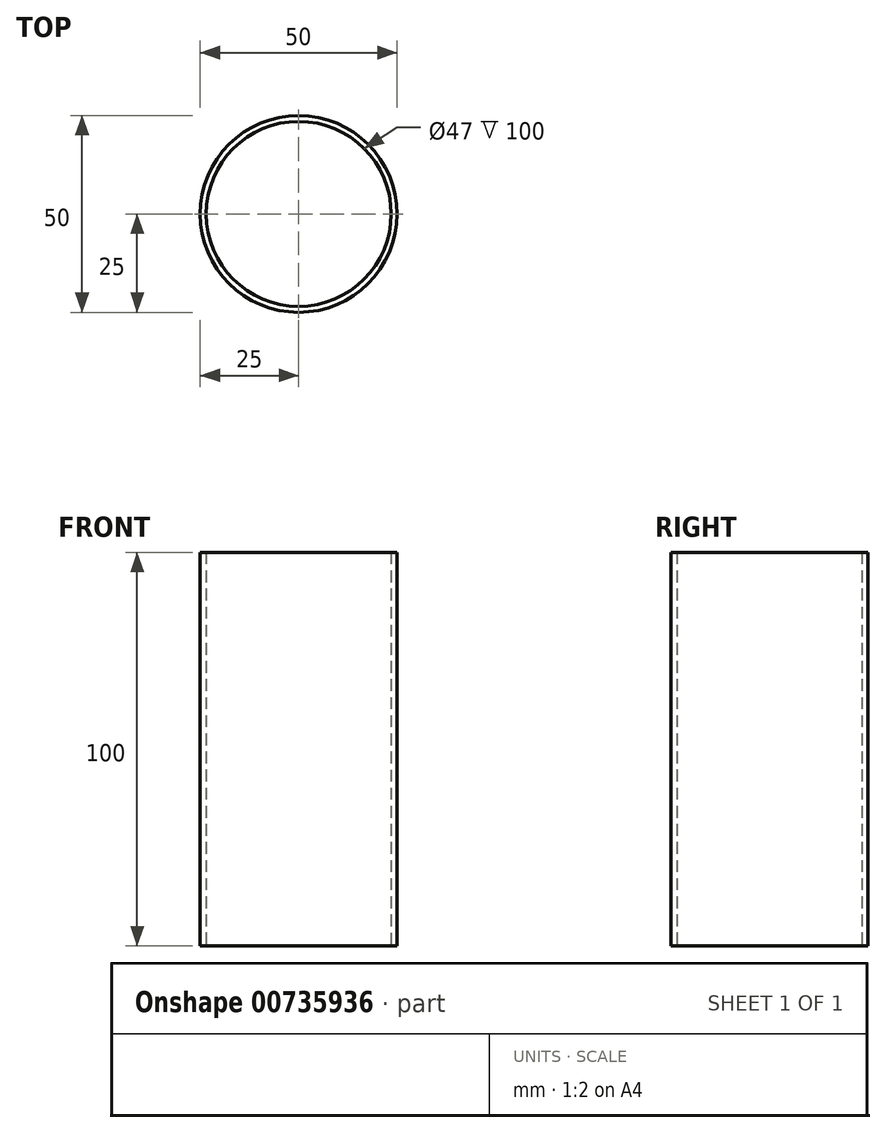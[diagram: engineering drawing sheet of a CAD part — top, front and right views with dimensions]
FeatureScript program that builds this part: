
annotation { "Feature Type Name" : "Feature", "Feature Type Description" : "" }
export const myFeature = defineFeature(function(context is Context, id is Id, definition is map)
    precondition{}
    {
        {
            var Q0;
            Q0=qCreatedBy(makeId("Top.planeOp"),FACE);
            var sketch = newSketch(context, id + "F0", { "sketchPlane" : qUnion([Q0])});
            skCircle(sketch, "E0", {"center": v(0, 0) * mm, "radius": 25 * mm});
            skCircle(sketch, "E1", {"center": v(0, 0) * mm, "radius": 23.5 * mm});
            skSolve(sketch);
        }
        {
            var Q0;
            Q0 = qSketchRegion(id + "F0", true);
            extrude(context, id + "F1", {"entities" : qUnion([Q0]), "depth" : 100 * mm, "offsetDistance" : 25 * mm});
        }
    });
